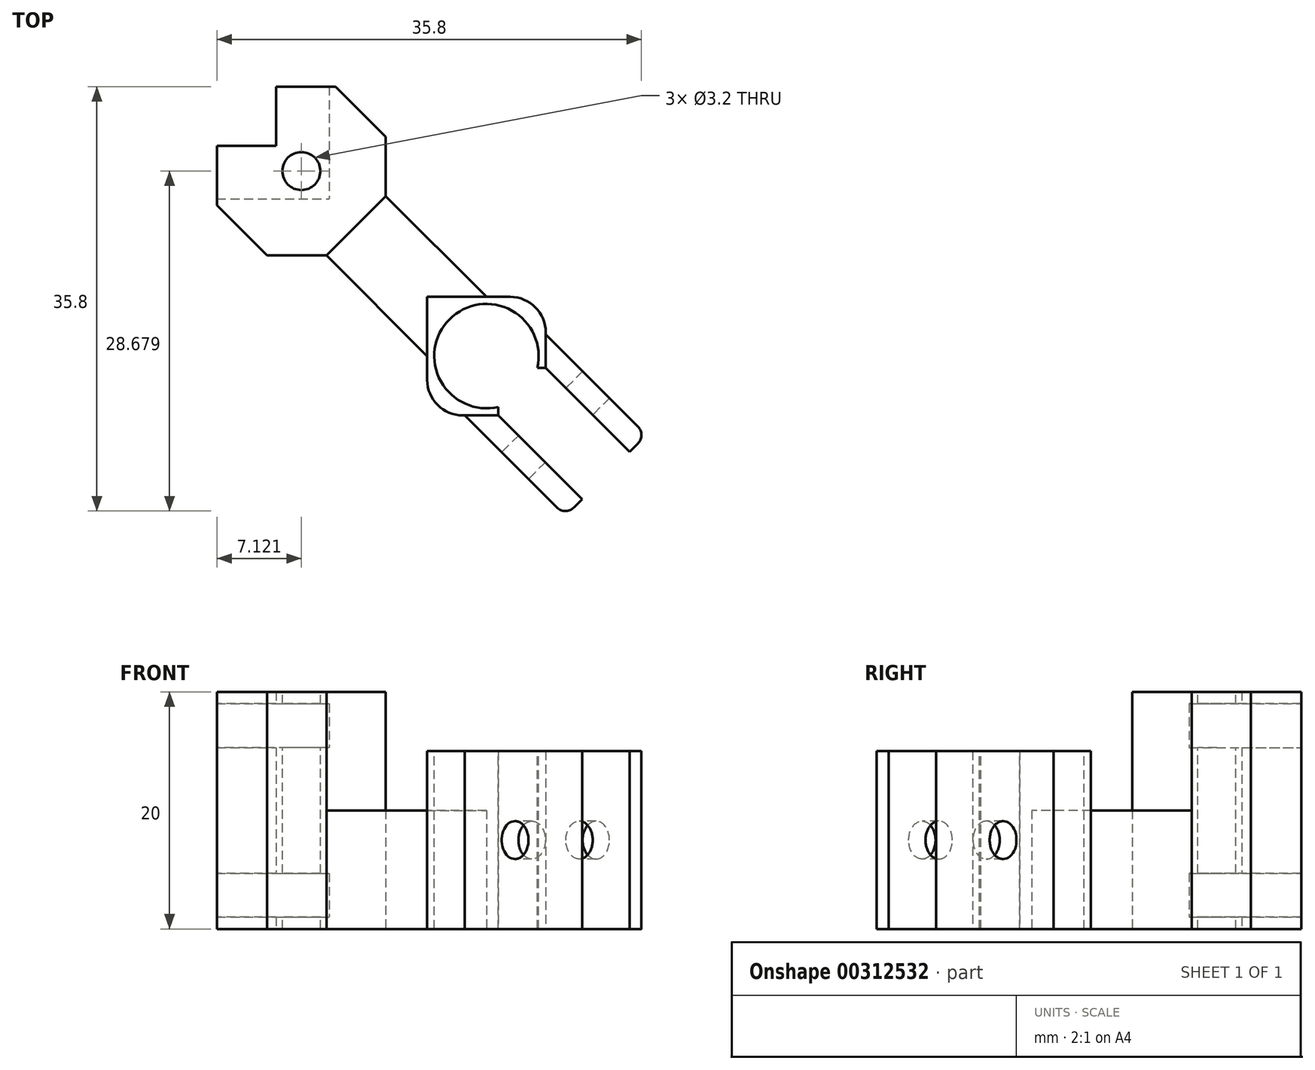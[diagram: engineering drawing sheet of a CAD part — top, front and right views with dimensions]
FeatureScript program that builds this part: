
annotation { "Feature Type Name" : "Feature", "Feature Type Description" : "" }
export const myFeature = defineFeature(function(context is Context, id is Id, definition is map)
    precondition{}
    {
        {
            var Q0;
            Q0=qCreatedBy(makeId("Top.planeOp"),FACE);
            var sketch = newSketch(context, id + "F0", { "sketchPlane" : qUnion([Q0])});
            skLineSegment(sketch, "E0", {"start": v(0, 0) * mm, "end": v(-5, 0) * mm});
            skLineSegment(sketch, "E1", {"start": v(-5, 0) * mm, "end": v(-5, 5) * mm});
            skLineSegment(sketch, "E2", {"start": v(-5, 5) * mm, "end": v(0, 5) * mm});
            skLineSegment(sketch, "E3", {"start": v(0, 5) * mm, "end": v(0, 10) * mm});
            skLineSegment(sketch, "E4", {"start": v(0, 10) * mm, "end": v(5, 10) * mm});
            skLineSegment(sketch, "E5", {"start": v(5, 10) * mm, "end": v(5, 5) * mm});
            skLineSegment(sketch, "E6", {"start": v(-5, 0) * mm, "end": v(-0.76, -4.24) * mm});
            skLineSegment(sketch, "E7", {"start": v(5, 10) * mm, "end": v(9.24, 5.76) * mm});
            skLineSegment(sketch, "E8", {"start": v(9.24, 5.76) * mm, "end": v(9.24, 0.76) * mm});
            skLineSegment(sketch, "E9", {"start": v(-0.76, -4.24) * mm, "end": v(4.24, -4.24) * mm});
            skLineSegment(sketch, "E10", {"start": v(9.24, 0.76) * mm, "end": v(17.73, -7.73) * mm});
            skLineSegment(sketch, "E11", {"start": v(4.24, -4.24) * mm, "end": v(12.73, -12.73) * mm});
            skLineSegment(sketch, "E12", {"start": v(12.73, -12.73) * mm, "end": v(12.73, -17.73) * mm});
            skLineSegment(sketch, "E13", {"start": v(12.73, -17.73) * mm, "end": v(22.73, -17.73) * mm});
            skLineSegment(sketch, "E14", {"start": v(22.73, -17.73) * mm, "end": v(22.73, -7.73) * mm});
            skLineSegment(sketch, "E15", {"start": v(22.73, -7.73) * mm, "end": v(17.73, -7.73) * mm});
            skLineSegment(sketch, "E16", {"start": v(4.24, -4.24) * mm, "end": v(9.24, 0.76) * mm});
            skPoint(sketch, "E17", {"position": v(22.73, -13.73) * mm});
            skPoint(sketch, "E18", {"position": v(18.73, -17.73) * mm});
            skLineSegment(sketch, "E19", {"start": v(22.73, -13.73) * mm, "end": v(29.8, -20.8) * mm});
            skLineSegment(sketch, "E20", {"start": v(18.73, -17.73) * mm, "end": v(25.8, -24.8) * mm});
            skLineSegment(sketch, "E21", {"start": v(29.8, -20.8) * mm, "end": v(31.21, -19.38) * mm});
            skLineSegment(sketch, "E22", {"start": v(31.21, -19.38) * mm, "end": v(22.73, -10.9) * mm});
            skLineSegment(sketch, "E23", {"start": v(25.8, -24.8) * mm, "end": v(24.38, -26.21) * mm});
            skLineSegment(sketch, "E24", {"start": v(24.38, -26.21) * mm, "end": v(15.9, -17.73) * mm});
            skSolve(sketch);
        }
        {
            var Q0;
            Q0=makeQuery(id+"F0.imprint","IMPRINT",FACE,{"disambiguationData":[TD([[makeQuery(id+"F0.imprint","IMPRINT",EDGE,{"derivedFrom":sQuery(id+"F0.wireOp",EDGE,"E1")}),-1.0]])]});
            extrude(context, id + "F1", {"entities" : qUnion([Q0]), "depth" : 20 * mm});
        }
        {
            var Q0;
            Q0=makeQuery(id+"F0.imprint","IMPRINT",FACE,{"disambiguationData":[TD([[makeQuery(id+"F0.imprint","IMPRINT",EDGE,{"derivedFrom":sQuery(id+"F0.wireOp",EDGE,"E10")}),-1.0]])]});
            extrude(context, id + "F2", {"entities" : qUnion([Q0]), "operationType" : NewBodyOperationType.ADD, "depth" : 10 * mm});
        }
        {
            var Q0;
            Q0=makeQuery(id+"F1.opExtrude","SWEPT_FACE",FACE,{"disambiguationData":[OSD([sQuery(id+"F0.wireOp",EDGE,"E4")])]});
            var sketch = newSketch(context, id + "F3", { "sketchPlane" : qUnion([Q0])});
            skPoint(sketch, "E25", {"position": v(0, 19) * mm});
            skPoint(sketch, "E26", {"position": v(0, 15.6) * mm});
            skPoint(sketch, "E27", {"position": v(0, 1) * mm});
            skPoint(sketch, "E28", {"position": v(0, 4.4) * mm});
            skLineSegment(sketch, "E29", {"start": v(0, 19) * mm, "end": v(-5, 19) * mm});
            skLineSegment(sketch, "E30", {"start": v(-5, 19) * mm, "end": v(-5, 15.6) * mm});
            skLineSegment(sketch, "E31", {"start": v(-5, 15.6) * mm, "end": v(0, 15.6) * mm});
            skSolve(sketch);
        }
        {
            var Q0;
            Q0=qSketchRegion(id+"F3",true);
            var Q1;
            {var subQ0=sQuery(id+"F3.wireOp",EDGE,"E29");Q1=makeQuery(id+"F3.imprint","IMPRINT",FACE,{"disambiguationData":[TD([[makeQuery(id+"F3.imprint","IMPRINT",EDGE,{"derivedFrom":subQ0}),1.0]])]});}
            extrude(context, id + "F4", {"entities" : qUnion([Q0, Q1]), "operationType" : NewBodyOperationType.REMOVE, "oppositeDirection" : true, "depth" : 25 * mm});
        }
        {
            var Q0;
            Q0=makeQuery(id+"F1.opExtrude","SWEPT_FACE",FACE,{"disambiguationData":[OSD([sQuery(id+"F0.wireOp",EDGE,"E2")])]});
            var sketch = newSketch(context, id + "F5", { "sketchPlane" : qUnion([Q0])});
            skLineSegment(sketch, "E32", {"start": v(0, 19) * mm, "end": v(5, 19) * mm});
            skLineSegment(sketch, "E33", {"start": v(5, 19) * mm, "end": v(5, 15.6) * mm});
            skLineSegment(sketch, "E34", {"start": v(5, 15.6) * mm, "end": v(0, 15.6) * mm});
            skLineSegment(sketch, "E35", {"start": v(0, 15.6) * mm, "end": v(0, 19) * mm});
            skSolve(sketch);
        }
        {
            var Q0;
            Q0=makeQuery(id+"F5.imprint","IMPRINT",FACE,{"disambiguationData":[TD([[makeQuery(id+"F5.imprint","IMPRINT",EDGE,{"derivedFrom":sQuery(id+"F5.wireOp",EDGE,"E32")}),-1.0]])]});
            extrude(context, id + "F6", {"entities" : qUnion([Q0]), "operationType" : NewBodyOperationType.REMOVE, "oppositeDirection" : true, "depth" : 25 * mm});
        }
        {
            var Q0;
            Q0=makeQuery(id+"F1.opExtrude","SWEPT_FACE",FACE,{"disambiguationData":[OSD([sQuery(id+"F0.wireOp",EDGE,"E7")])]});
            var sketch = newSketch(context, id + "F7", { "sketchPlane" : qUnion([Q0])});
            skLineSegment(sketch, "E36", {"start": v(3.54, 15.6) * mm, "end": v(-2.46, 15.6) * mm});
            skLineSegment(sketch, "E37", {"start": v(-2.46, 15.6) * mm, "end": v(-2.46, 19) * mm});
            skLineSegment(sketch, "E38", {"start": v(-2.46, 19) * mm, "end": v(3.54, 19) * mm});
            skLineSegment(sketch, "E39", {"start": v(3.54, 19) * mm, "end": v(3.54, 15.6) * mm});
            skSolve(sketch);
        }
        {
            var Q0;
            Q0=qSketchRegion(id+"F7",true);
            extrude(context, id + "F8", {"entities" : qUnion([Q0]), "operationType" : NewBodyOperationType.REMOVE, "oppositeDirection" : true, "depth" : 25 * mm});
        }
        {
            var Q0;
            {var subQ3=sQuery(id+"F0.wireOp",EDGE,"E4");Q0=makeQuery(id+"F4.boolean.opBoolean","SPLIT",FACE,{"disambiguationData":[TD([makeQuery(id+"F4.opExtrude","SWEPT_FACE",FACE,{"disambiguationData":[OSD([sQuery(id+"F3.wireOp",EDGE,"E31")])]})])],"derivedFrom":makeQuery(id+"F1.opExtrude","SWEPT_FACE",FACE,{"disambiguationData":[OSD([subQ3])]})});}
            var sketch = newSketch(context, id + "F9", { "sketchPlane" : qUnion([Q0])});
            skPoint(sketch, "E40", {"position": v(0, 1) * mm});
            skPoint(sketch, "E41", {"position": v(0, 4.4) * mm});
            skLineSegment(sketch, "E42.bottom", {"start": v(0, 4.4) * mm, "end": v(-5, 4.4) * mm});
            skLineSegment(sketch, "E42.top", {"start": v(0, 1) * mm, "end": v(-5, 1) * mm});
            skLineSegment(sketch, "E42.left", {"start": v(0, 4.4) * mm, "end": v(0, 1) * mm});
            skLineSegment(sketch, "E42.right", {"start": v(-5, 4.4) * mm, "end": v(-5, 1) * mm});
            skSolve(sketch);
        }
        {
            var Q0;
            Q0=qSketchRegion(id+"F9",true);
            extrude(context, id + "F10", {"entities" : qUnion([Q0]), "operationType" : NewBodyOperationType.REMOVE, "oppositeDirection" : true, "depth" : 25 * mm});
        }
        {
            var Q0;
            {var subQ3=sQuery(id+"F0.wireOp",EDGE,"E7");Q0=makeQuery(id+"F8.boolean.opBoolean","SPLIT",FACE,{"disambiguationData":[TD([makeQuery(id+"F4.boolean.opBoolean","COPY",FACE,{"derivedFrom":makeQuery(id+"F4.opExtrude","SWEPT_FACE",FACE,{"disambiguationData":[OSD([sQuery(id+"F3.wireOp",EDGE,"E31")])]})})])],"derivedFrom":makeQuery(id+"F1.opExtrude","SWEPT_FACE",FACE,{"disambiguationData":[OSD([subQ3])]})});}
            var sketch = newSketch(context, id + "F11", { "sketchPlane" : qUnion([Q0])});
            skLineSegment(sketch, "E43.bottom", {"start": v(3.54, 1) * mm, "end": v(-2.46, 1) * mm});
            skLineSegment(sketch, "E43.top", {"start": v(3.54, 4.4) * mm, "end": v(-2.46, 4.4) * mm});
            skLineSegment(sketch, "E43.left", {"start": v(3.54, 1) * mm, "end": v(3.54, 4.4) * mm});
            skLineSegment(sketch, "E43.right", {"start": v(-2.46, 1) * mm, "end": v(-2.46, 4.4) * mm});
            skSolve(sketch);
        }
        {
            var Q0;
            Q0=qSketchRegion(id+"F11",true);
            extrude(context, id + "F12", {"entities" : qUnion([Q0]), "operationType" : NewBodyOperationType.REMOVE, "oppositeDirection" : true, "depth" : 25 * mm});
        }
        {
            var Q0;
            {var subQ2=sQuery(id+"F0.wireOp",EDGE,"E2");Q0=makeQuery(id+"F6.boolean.opBoolean","SPLIT",FACE,{"disambiguationData":[TD([makeQuery(id+"F4.boolean.opBoolean","COPY",FACE,{"derivedFrom":makeQuery(id+"F4.opExtrude","SWEPT_FACE",FACE,{"disambiguationData":[OSD([sQuery(id+"F3.wireOp",EDGE,"E31")])]})})])],"derivedFrom":makeQuery(id+"F1.opExtrude","SWEPT_FACE",FACE,{"disambiguationData":[OSD([subQ2])]})});}
            var sketch = newSketch(context, id + "F13", { "sketchPlane" : qUnion([Q0])});
            skLineSegment(sketch, "E44.bottom", {"start": v(0, 4.4) * mm, "end": v(5, 4.4) * mm});
            skLineSegment(sketch, "E44.top", {"start": v(0, 1) * mm, "end": v(5, 1) * mm});
            skLineSegment(sketch, "E44.left", {"start": v(0, 4.4) * mm, "end": v(0, 1) * mm});
            skLineSegment(sketch, "E44.right", {"start": v(5, 4.4) * mm, "end": v(5, 1) * mm});
            skSolve(sketch);
        }
        {
            var Q0;
            Q0=qSketchRegion(id+"F13",true);
            extrude(context, id + "F14", {"entities" : qUnion([Q0]), "operationType" : NewBodyOperationType.REMOVE, "oppositeDirection" : true, "depth" : 25 * mm});
        }
        {
            var Q0;
            Q0=makeQuery(id+"F1.opExtrude","CAP_FACE",FACE,{"disambiguationData":[OSD([sQuery(id+"F0.wireOp",EDGE,"E1"),sQuery(id+"F0.wireOp",EDGE,"E2"),sQuery(id+"F0.wireOp",EDGE,"E3"),sQuery(id+"F0.wireOp",EDGE,"E4"),sQuery(id+"F0.wireOp",EDGE,"E6"),sQuery(id+"F0.wireOp",EDGE,"E7"),sQuery(id+"F0.wireOp",EDGE,"E8"),sQuery(id+"F0.wireOp",EDGE,"E9"),sQuery(id+"F0.wireOp",EDGE,"E16")])],"isStart":false});
            var sketch = newSketch(context, id + "F15", { "sketchPlane" : qUnion([Q0])});
            skLineSegment(sketch, "E45", {"start": v(0, 5) * mm, "end": v(0, 3.17) * mm});
            skLineSegment(sketch, "E46", {"start": v(0, 5) * mm, "end": v(2.05, 5) * mm});
            skLineSegment(sketch, "E47", {"start": v(0, 5) * mm, "end": v(2.12, 2.88) * mm});
            skSolve(sketch);
        }
        {
            var Q0;
            Q0=sQuery(id+"F15.wireOp",VERTEX,"E47.end");
            var Q1;
            Q1=makeQuery(id+"F1.opExtrude","SWEPT_BODY",BODY,{"disambiguationData":[OSD([sQuery(id+"F0.wireOp",EDGE,"E1"),sQuery(id+"F0.wireOp",EDGE,"E2"),sQuery(id+"F0.wireOp",EDGE,"E3"),sQuery(id+"F0.wireOp",EDGE,"E4"),sQuery(id+"F0.wireOp",EDGE,"E6"),sQuery(id+"F0.wireOp",EDGE,"E7"),sQuery(id+"F0.wireOp",EDGE,"E8"),sQuery(id+"F0.wireOp",EDGE,"E9"),sQuery(id+"F0.wireOp",EDGE,"E16")])]});
            hole(context, id + "F16", {"style" : HoleStyle.SIMPLE, "endStyle" : HoleEndStyle.THROUGH, "holeDiameter" : 3.2 * mm, "tappedDepth" : 12 * mm, "tapClearance" : 3, "locations" : qUnion([Q0]), "scope" : qUnion([Q1])});
        }
        {
            var Q0;
            Q0=makeQuery(id+"F2.opExtrude","CAP_FACE",FACE,{"disambiguationData":[OSD([sQuery(id+"F0.wireOp",EDGE,"E10"),sQuery(id+"F0.wireOp",EDGE,"E11"),sQuery(id+"F0.wireOp",EDGE,"E12"),sQuery(id+"F0.wireOp",EDGE,"E13"),sQuery(id+"F0.wireOp",EDGE,"E14"),sQuery(id+"F0.wireOp",EDGE,"E15"),sQuery(id+"F0.wireOp",EDGE,"E16")])],"isStart":false});
            var sketch = newSketch(context, id + "F17", { "sketchPlane" : qUnion([Q0])});
            skLineSegment(sketch, "E48", {"start": v(22.73, -7.73) * mm, "end": v(12.73, -17.73) * mm});
            skLineSegment(sketch, "E49", {"start": v(22.73, -17.73) * mm, "end": v(13.62, -8.62) * mm});
            skPoint(sketch, "E50", {"position": v(17.73, -12.73) * mm});
            skSolve(sketch);
        }
        {
            var Q0;
            Q0=sQuery(id+"F17.wireOp",VERTEX,"E50");
            var Q1;
            Q1=makeQuery(id+"F1.opExtrude","SWEPT_BODY",BODY,{"disambiguationData":[OSD([sQuery(id+"F0.wireOp",EDGE,"E1"),sQuery(id+"F0.wireOp",EDGE,"E2"),sQuery(id+"F0.wireOp",EDGE,"E3"),sQuery(id+"F0.wireOp",EDGE,"E4"),sQuery(id+"F0.wireOp",EDGE,"E6"),sQuery(id+"F0.wireOp",EDGE,"E7"),sQuery(id+"F0.wireOp",EDGE,"E8"),sQuery(id+"F0.wireOp",EDGE,"E9"),sQuery(id+"F0.wireOp",EDGE,"E16")])]});
            hole(context, id + "F18", {"style" : HoleStyle.SIMPLE, "endStyle" : HoleEndStyle.THROUGH, "holeDiameter" : 8.8 * mm, "tappedDepth" : 12 * mm, "tapClearance" : 3, "locations" : qUnion([Q0]), "scope" : qUnion([Q1])});
        }
        {
            var Q0;
            Q0=makeQuery(id+"F2.opExtrude","CAP_FACE",FACE,{"disambiguationData":[OSD([sQuery(id+"F0.wireOp",EDGE,"E10"),sQuery(id+"F0.wireOp",EDGE,"E11"),sQuery(id+"F0.wireOp",EDGE,"E12"),sQuery(id+"F0.wireOp",EDGE,"E13"),sQuery(id+"F0.wireOp",EDGE,"E14"),sQuery(id+"F0.wireOp",EDGE,"E15"),sQuery(id+"F0.wireOp",EDGE,"E16")])],"isStart":false});
            var sketch = newSketch(context, id + "F19", { "sketchPlane" : qUnion([Q0])});
            skLineSegment(sketch, "E51.bottom", {"start": v(22.73, -7.73) * mm, "end": v(12.73, -7.73) * mm});
            skLineSegment(sketch, "E51.top", {"start": v(22.73, -17.73) * mm, "end": v(12.73, -17.73) * mm});
            skLineSegment(sketch, "E51.left", {"start": v(22.73, -7.73) * mm, "end": v(22.73, -17.73) * mm});
            skLineSegment(sketch, "E51.right", {"start": v(12.73, -7.73) * mm, "end": v(12.73, -17.73) * mm});
            skSolve(sketch);
        }
        {
            var Q0;
            {var subQ1=sQuery(id+"F19.wireOp",EDGE,"E51.top");Q0=makeQuery(id+"F19.imprint","IMPRINT",FACE,{"disambiguationData":[TD([[makeQuery(id+"F19.imprint","IMPRINT",EDGE,{"derivedFrom":subQ1}),1.0]])]});}
            extrude(context, id + "F20", {"entities" : qUnion([Q0]), "operationType" : NewBodyOperationType.ADD, "depth" : 5 * mm});
        }
        {
            var Q0;
            Q0=makeQuery(id+"F8.boolean.opBoolean","MERGE",FACE,{"derivedFrom":[makeQuery(id+"F6.boolean.opBoolean","MERGE",FACE,{"derivedFrom":[makeQuery(id+"F4.boolean.opBoolean","COPY",FACE,{"derivedFrom":makeQuery(id+"F4.opExtrude","SWEPT_FACE",FACE,{"disambiguationData":[OSD([sQuery(id+"F3.wireOp",EDGE,"E31")])]})}),makeQuery(id+"F6.opExtrude","SWEPT_FACE",FACE,{"disambiguationData":[OSD([sQuery(id+"F5.wireOp",EDGE,"E34")])]})]}),makeQuery(id+"F8.opExtrude","SWEPT_FACE",FACE,{"disambiguationData":[OSD([sQuery(id+"F7.wireOp",EDGE,"E36")])]})]});
            extrude(context, id + "F21", {"entities" : qUnion([Q0]), "operationType" : NewBodyOperationType.REMOVE, "oppositeDirection" : true, "depth" : 0.3 * mm});
        }
        {
            var Q0;
            Q0=makeQuery(id+"F14.boolean.opBoolean","MERGE",FACE,{"derivedFrom":[makeQuery(id+"F12.boolean.opBoolean","MERGE",FACE,{"derivedFrom":[makeQuery(id+"F10.boolean.opBoolean","COPY",FACE,{"derivedFrom":makeQuery(id+"F10.opExtrude","SWEPT_FACE",FACE,{"disambiguationData":[OSD([sQuery(id+"F9.wireOp",EDGE,"E42.bottom")])]})}),makeQuery(id+"F12.opExtrude","SWEPT_FACE",FACE,{"disambiguationData":[OSD([sQuery(id+"F11.wireOp",EDGE,"E43.top")])]})]}),makeQuery(id+"F14.opExtrude","SWEPT_FACE",FACE,{"disambiguationData":[OSD([sQuery(id+"F13.wireOp",EDGE,"E44.bottom")])]})]});
            extrude(context, id + "F22", {"entities" : qUnion([Q0]), "operationType" : NewBodyOperationType.REMOVE, "oppositeDirection" : true, "depth" : 0.3 * mm});
        }
        {
            var Q0;
            Q0=makeQuery(id+"F20.boolean.opBoolean","MERGE",FACE,{"derivedFrom":[makeQuery(id+"F2.opExtrude","SWEPT_FACE",FACE,{"disambiguationData":[OSD([sQuery(id+"F0.wireOp",EDGE,"E13")])]}),makeQuery(id+"F20.opExtrude","SWEPT_FACE",FACE,{"disambiguationData":[OSD([sQuery(id+"F19.wireOp",EDGE,"E51.top")])]})]});
            var sketch = newSketch(context, id + "F23", { "sketchPlane" : qUnion([Q0])});
            skLineSegment(sketch, "E52", {"start": v(12.79, 15) * mm, "end": v(22.73, 15) * mm});
            skPoint(sketch, "E53", {"position": v(18.73, 15) * mm});
            skLineSegment(sketch, "E54", {"start": v(18.73, 15) * mm, "end": v(18.73, 0) * mm});
            skLineSegment(sketch, "E55", {"start": v(18.73, 0) * mm, "end": v(22.73, 0) * mm});
            skLineSegment(sketch, "E56", {"start": v(22.73, 0) * mm, "end": v(22.73, 15) * mm});
            skSolve(sketch);
        }
        {
            var Q0;
            Q0=makeQuery(id+"F20.boolean.opBoolean","MERGE",FACE,{"derivedFrom":[makeQuery(id+"F2.opExtrude","SWEPT_FACE",FACE,{"disambiguationData":[OSD([sQuery(id+"F0.wireOp",EDGE,"E14")])]}),makeQuery(id+"F20.opExtrude","SWEPT_FACE",FACE,{"disambiguationData":[OSD([sQuery(id+"F19.wireOp",EDGE,"E51.left")])]})]});
            var sketch = newSketch(context, id + "F24", { "sketchPlane" : qUnion([Q0])});
            skLineSegment(sketch, "E57", {"start": v(-17.73, 15) * mm, "end": v(-7.73, 15) * mm});
            skPoint(sketch, "E58", {"position": v(-13.73, 15) * mm});
            skLineSegment(sketch, "E59", {"start": v(-13.73, 15) * mm, "end": v(-13.73, 0) * mm});
            skLineSegment(sketch, "E60", {"start": v(-13.73, 0) * mm, "end": v(-17.73, 0) * mm});
            skLineSegment(sketch, "E61", {"start": v(-17.73, 0) * mm, "end": v(-17.73, 15) * mm});
            skSolve(sketch);
        }
        {
            var Q0;
            Q0=qSketchRegion(id+"F24",true);
            extrude(context, id + "F25", {"entities" : qUnion([Q0]), "operationType" : NewBodyOperationType.REMOVE, "oppositeDirection" : true, "depth" : 2.4 * mm});
        }
        {
            var Q0;
            Q0=qSketchRegion(id+"F23",true);
            extrude(context, id + "F26", {"entities" : qUnion([Q0]), "operationType" : NewBodyOperationType.REMOVE, "oppositeDirection" : true, "depth" : 3.85 * mm});
        }
        {
            var Q0;
            {var subQ0=sQuery(id+"F0.wireOp",EDGE,"E19");Q0=makeQuery(id+"F0.imprint","IMPRINT",FACE,{"disambiguationData":[TD([[makeQuery(id+"F0.imprint","IMPRINT",EDGE,{"derivedFrom":subQ0}),1.0]])]});}
            var Q1;
            {var subQ0=sQuery(id+"F0.wireOp",EDGE,"E20");Q1=makeQuery(id+"F0.imprint","IMPRINT",FACE,{"disambiguationData":[TD([[makeQuery(id+"F0.imprint","IMPRINT",EDGE,{"derivedFrom":subQ0}),-1.0]])]});}
            extrude(context, id + "F27", {"entities" : qUnion([Q0, Q1]), "depth" : 16.99 * mm});
        }
        {
            var Q0;
            Q0=makeQuery(id+"F27.opExtrude","CAP_FACE",FACE,{"disambiguationData":[OSD([sQuery(id+"F0.wireOp",EDGE,"E13"),sQuery(id+"F0.wireOp",EDGE,"E20"),sQuery(id+"F0.wireOp",EDGE,"E23"),sQuery(id+"F0.wireOp",EDGE,"E24")])],"isStart":false});
            extrude(context, id + "F28", {"entities" : qUnion([Q0]), "operationType" : NewBodyOperationType.REMOVE, "oppositeDirection" : true, "depth" : 2 * mm});
        }
        {
            var Q0;
            Q0=makeQuery(id+"F27.opExtrude","CAP_FACE",FACE,{"disambiguationData":[OSD([sQuery(id+"F0.wireOp",EDGE,"E14"),sQuery(id+"F0.wireOp",EDGE,"E19"),sQuery(id+"F0.wireOp",EDGE,"E21"),sQuery(id+"F0.wireOp",EDGE,"E22")])],"isStart":false});
            extrude(context, id + "F29", {"entities" : qUnion([Q0]), "operationType" : NewBodyOperationType.REMOVE, "oppositeDirection" : true, "depth" : 2 * mm});
        }
        {
            var Q0;
            Q0=makeQuery(id+"F27.opExtrude","SWEPT_FACE",FACE,{"disambiguationData":[OSD([sQuery(id+"F0.wireOp",EDGE,"E24")])]});
            var sketch = newSketch(context, id + "F30", { "sketchPlane" : qUnion([Q0])});
            skLineSegment(sketch, "E62", {"start": v(35.78, 15) * mm, "end": v(23.78, 0) * mm});
            skLineSegment(sketch, "E63", {"start": v(23.78, 15) * mm, "end": v(35.78, 0) * mm});
            skPoint(sketch, "E64", {"position": v(29.78, 7.5) * mm});
            skSolve(sketch);
        }
        {
            var Q0;
            Q0=sQuery(id+"F30.wireOp",VERTEX,"E64");
            var Q1;
            Q1=makeQuery(id+"F27.opExtrude","SWEPT_BODY",BODY,{"disambiguationData":[OSD([sQuery(id+"F0.wireOp",EDGE,"E13"),sQuery(id+"F0.wireOp",EDGE,"E20"),sQuery(id+"F0.wireOp",EDGE,"E23"),sQuery(id+"F0.wireOp",EDGE,"E24")])]});
            var Q2;
            Q2=makeQuery(id+"F27.opExtrude","SWEPT_BODY",BODY,{"disambiguationData":[OSD([sQuery(id+"F0.wireOp",EDGE,"E14"),sQuery(id+"F0.wireOp",EDGE,"E19"),sQuery(id+"F0.wireOp",EDGE,"E21"),sQuery(id+"F0.wireOp",EDGE,"E22")])]});
            hole(context, id + "F31", {"style" : HoleStyle.SIMPLE, "endStyle" : HoleEndStyle.THROUGH, "holeDiameter" : 3.2 * mm, "tappedDepth" : 12 * mm, "tapClearance" : 3, "locations" : qUnion([Q0]), "scope" : qUnion([Q1, Q2])});
        }
        {
            var Q0;
            Q0=makeQuery(id+"F20.boolean.opBoolean","MERGE",EDGE,{"derivedFrom":[makeQuery(id+"F2.opExtrude","SWEPT_EDGE",EDGE,{"disambiguationData":[OSD([sQuery(id+"F0.wireOp",EDGE,"E14"),sQuery(id+"F0.wireOp",EDGE,"E15")])]}),makeQuery(id+"F20.opExtrude","SWEPT_EDGE",EDGE,{"disambiguationData":[OSD([sQuery(id+"F19.wireOp",EDGE,"E51.bottom"),sQuery(id+"F19.wireOp",EDGE,"E51.left")])]})]});
            fillet(context, id + "F32", {"entities" : qUnion([Q0]), "radius" : 3 * mm, "tangentPropagation" : true, "allowEdgeOverflow" : false});
        }
        {
            var Q0;
            Q0=makeQuery(id+"F20.boolean.opBoolean","MERGE",EDGE,{"derivedFrom":[makeQuery(id+"F2.opExtrude","SWEPT_EDGE",EDGE,{"disambiguationData":[OSD([sQuery(id+"F0.wireOp",EDGE,"E12"),sQuery(id+"F0.wireOp",EDGE,"E13")])]}),makeQuery(id+"F20.opExtrude","SWEPT_EDGE",EDGE,{"disambiguationData":[OSD([sQuery(id+"F19.wireOp",EDGE,"E51.top"),sQuery(id+"F19.wireOp",EDGE,"E51.right")])]})]});
            fillet(context, id + "F33", {"entities" : qUnion([Q0]), "radius" : 3 * mm, "tangentPropagation" : true, "allowEdgeOverflow" : false});
        }
        {
            var Q0;
            Q0=makeQuery(id+"F27.opExtrude","SWEPT_EDGE",EDGE,{"disambiguationData":[OSD([sQuery(id+"F0.wireOp",EDGE,"E23"),sQuery(id+"F0.wireOp",EDGE,"E24")])]});
            fillet(context, id + "F34", {"entities" : qUnion([Q0]), "radius" : 1 * mm, "tangentPropagation" : true, "allowEdgeOverflow" : false});
        }
        {
            var Q0;
            Q0=makeQuery(id+"F27.opExtrude","SWEPT_EDGE",EDGE,{"disambiguationData":[OSD([sQuery(id+"F0.wireOp",EDGE,"E21"),sQuery(id+"F0.wireOp",EDGE,"E22")])]});
            fillet(context, id + "F35", {"entities" : qUnion([Q0]), "radius" : 1 * mm, "tangentPropagation" : true, "allowEdgeOverflow" : false});
        }
        {
            var Q0;
            Q0=makeQuery(id+"F21.boolean.opBoolean","COPY",FACE,{"derivedFrom":makeQuery(id+"F21.opExtrude","CAP_FACE",FACE,{"disambiguationData":[OSD([sQuery(id+"F3.wireOp",EDGE,"E31"),sQuery(id+"F5.wireOp",EDGE,"E34"),sQuery(id+"F7.wireOp",EDGE,"E36")])],"isStart":false})});
            var sketch = newSketch(context, id + "F36", { "sketchPlane" : qUnion([Q0])});
            skLineSegment(sketch, "E65", {"start": v(4.45, 0.55) * mm, "end": v(-5, 0.55) * mm});
            skLineSegment(sketch, "E66", {"start": v(4.45, 0.55) * mm, "end": v(4.45, 10) * mm});
            skSolve(sketch);
        }
        {
            var Q0;
            {var subQ6=sQuery(id+"F36.wireOp",EDGE,"E65");Q0=makeQuery(id+"F36.imprint","IMPRINT",FACE,{"disambiguationData":[TD([[makeQuery(id+"F36.imprint","IMPRINT",EDGE,{"derivedFrom":subQ6}),1.0]])]});}
            extrude(context, id + "F37", {"entities" : qUnion([Q0]), "operationType" : NewBodyOperationType.ADD, "depth" : 4 * mm, "hasSecondDirection" : true, "secondDirectionOppositeDirection" : true, "secondDirectionDepth" : 14.72 * mm});
        }
        {
            var Q0;
            {var subQ1=sQuery(id+"F0.wireOp",EDGE,"E9");Q0=makeQuery(id+"F37.boolean.opBoolean","SPLIT",FACE,{"disambiguationData":[TD([makeQuery(id+"F1.opExtrude","SWEPT_FACE",FACE,{"disambiguationData":[OSD([subQ1])]})])],"derivedFrom":makeQuery(id+"F14.boolean.opBoolean","MERGE",FACE,{"derivedFrom":[makeQuery(id+"F12.boolean.opBoolean","MERGE",FACE,{"derivedFrom":[makeQuery(id+"F10.boolean.opBoolean","COPY",FACE,{"derivedFrom":makeQuery(id+"F10.opExtrude","SWEPT_FACE",FACE,{"disambiguationData":[OSD([sQuery(id+"F9.wireOp",EDGE,"E42.top")])]})}),makeQuery(id+"F12.opExtrude","SWEPT_FACE",FACE,{"disambiguationData":[OSD([sQuery(id+"F11.wireOp",EDGE,"E43.bottom")])]})]}),makeQuery(id+"F14.opExtrude","SWEPT_FACE",FACE,{"disambiguationData":[OSD([sQuery(id+"F13.wireOp",EDGE,"E44.top")])]})]})});}
            extrude(context, id + "F38", {"entities" : qUnion([Q0]), "operationType" : NewBodyOperationType.ADD, "depth" : 4.73 * mm});
        }
    });
